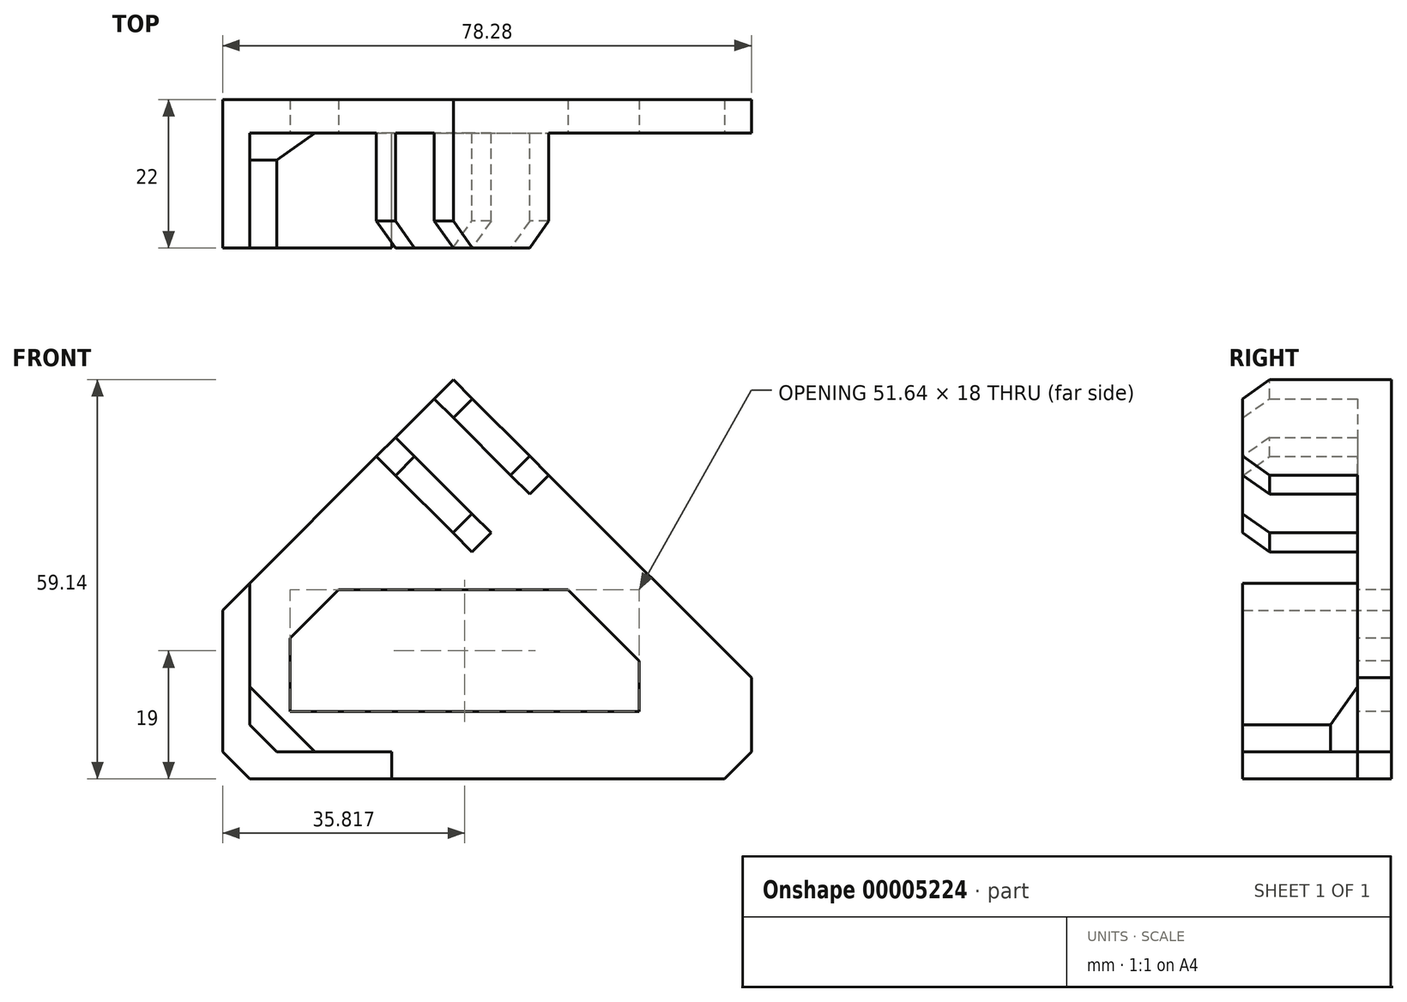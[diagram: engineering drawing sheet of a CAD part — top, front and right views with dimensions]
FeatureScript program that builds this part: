
annotation { "Feature Type Name" : "Feature", "Feature Type Description" : "" }
export const myFeature = defineFeature(function(context is Context, id is Id, definition is map)
    precondition{}
    {
        {
            var Q0;
            Q0=qCreatedBy(makeId("Front.planeOp"),FACE);
            var sketch = newSketch(context, id + "F0", { "sketchPlane" : qUnion([Q0])});
            skLineSegment(sketch, "E0", {"start": v(0, 0) * mm, "end": v(-75.51, 75.51) * mm, "construction": true});
            skLineSegment(sketch, "E1", {"start": v(0, 0) * mm, "end": v(-130.95, 0) * mm, "construction": true});
            skLineSegment(sketch, "E2", {"start": v(-59.14, 59.14) * mm, "end": v(-93.28, 25) * mm});
            skLineSegment(sketch, "E3", {"start": v(-93.28, 25) * mm, "end": v(-93.28, 0) * mm});
            skLineSegment(sketch, "E4", {"start": v(-93.28, 0) * mm, "end": v(-15, 0) * mm});
            skLineSegment(sketch, "E5", {"start": v(-15, 0) * mm, "end": v(-15, 15) * mm});
            skLineSegment(sketch, "E6", {"start": v(-15, 15) * mm, "end": v(-59.14, 59.14) * mm});
            skPoint(sketch, "E7", {"position": v(-45, 45) * mm});
            skSolve(sketch);
        }
        {
            var Q0;
            Q0 = qSketchRegion(id + "F0", true);
            extrude(context, id + "F1", {"entities" : qUnion([Q0]), "depth" : 5 * mm});
        }
        {
            var Q0;
            Q0=makeQuery(id+"F1.opExtrude","CAP_FACE",FACE,{"disambiguationData":[OSD([sQuery(id+"F0.wireOp",EDGE,"E2"),sQuery(id+"F0.wireOp",EDGE,"E3"),sQuery(id+"F0.wireOp",EDGE,"E4"),sQuery(id+"F0.wireOp",EDGE,"E5"),sQuery(id+"F0.wireOp",EDGE,"E6")])],"isStart":false});
            var sketch = newSketch(context, id + "F2", { "sketchPlane" : qUnion([Q0])});
            skLineSegment(sketch, "E8", {"start": v(-59.14, 59.14) * mm, "end": v(-61.97, 56.31) * mm});
            skLineSegment(sketch, "E9", {"start": v(-61.97, 56.31) * mm, "end": v(-47.83, 42.17) * mm});
            skLineSegment(sketch, "E10", {"start": v(-47.83, 42.17) * mm, "end": v(-45, 45) * mm});
            skLineSegment(sketch, "E11", {"start": v(-45, 45) * mm, "end": v(-59.14, 59.14) * mm});
            skLineSegment(sketch, "E12", {"start": v(-64.83, 53.45) * mm, "end": v(-26.8, 15.42) * mm, "construction": true});
            skLineSegment(sketch, "E13.MirrorCS", {"start": v(-70.53, 47.76) * mm, "end": v(-67.7, 50.59) * mm});
            skLineSegment(sketch, "E14.MirrorCS", {"start": v(-56.38, 33.62) * mm, "end": v(-70.53, 47.76) * mm});
            skLineSegment(sketch, "E15.MirrorCS", {"start": v(-53.56, 36.44) * mm, "end": v(-56.38, 33.62) * mm});
            skLineSegment(sketch, "E16.MirrorCS", {"start": v(-67.7, 50.59) * mm, "end": v(-53.56, 36.44) * mm});
            skLineSegment(sketch, "E17", {"start": v(-93.28, 25) * mm, "end": v(-93.28, 0) * mm});
            skLineSegment(sketch, "E18", {"start": v(-93.28, 0) * mm, "end": v(-68.28, 0) * mm});
            skLineSegment(sketch, "E19", {"start": v(-68.28, 0) * mm, "end": v(-68.28, 4) * mm});
            skLineSegment(sketch, "E20", {"start": v(-68.28, 4) * mm, "end": v(-89.28, 4) * mm});
            skLineSegment(sketch, "E21", {"start": v(-89.28, 4) * mm, "end": v(-89.28, 29) * mm});
            skLineSegment(sketch, "E22", {"start": v(-89.28, 29) * mm, "end": v(-93.28, 25) * mm});
            skSolve(sketch);
        }
        {
            var Q0;
            Q0 = qSketchRegion(id + "F2", true);
            extrude(context, id + "F3", {"entities" : qUnion([Q0]), "operationType" : NewBodyOperationType.ADD, "depth" : 17 * mm});
        }
        {
            var Q0;
            Q0=makeQuery(id+"F3.opExtrude","CAP_EDGE",EDGE,{"disambiguationData":[OSD([sQuery(id+"F2.wireOp",EDGE,"E8")])],"isStart":false});
            var Q1;
            Q1=makeQuery(id+"F3.opExtrude","CAP_EDGE",EDGE,{"disambiguationData":[OSD([sQuery(id+"F2.wireOp",EDGE,"E10")])],"isStart":false});
            var Q2;
            Q2=makeQuery(id+"F3.opExtrude","CAP_EDGE",EDGE,{"disambiguationData":[OSD([sQuery(id+"F2.wireOp",EDGE,"E13.MirrorCS")])],"isStart":false});
            var Q3;
            Q3=makeQuery(id+"F3.opExtrude","CAP_EDGE",EDGE,{"disambiguationData":[OSD([sQuery(id+"F2.wireOp",EDGE,"E15.MirrorCS")])],"isStart":false});
            var Q4;
            Q4=makeQuery(id+"F1.opExtrude","SWEPT_EDGE",EDGE,{"disambiguationData":[OSD([sQuery(id+"F0.wireOp",EDGE,"E4"),sQuery(id+"F0.wireOp",EDGE,"E5")])]});
            var Q5;
            Q5=makeQuery(id+"F1.opExtrude","SWEPT_EDGE",EDGE,{"disambiguationData":[OSD([sQuery(id+"F0.wireOp",EDGE,"E3"),sQuery(id+"F0.wireOp",EDGE,"E4")])]});
            var Q6;
            Q6=makeQuery(id+"F3.opExtrude","CAP_EDGE",EDGE,{"disambiguationData":[OSD([sQuery(id+"F2.wireOp",EDGE,"E14.MirrorCS")])],"isStart":true});
            var Q7;
            Q7=makeQuery(id+"F3.opExtrude","SWEPT_EDGE",EDGE,{"disambiguationData":[OSD([sQuery(id+"F2.wireOp",EDGE,"E20"),sQuery(id+"F2.wireOp",EDGE,"E21")])]});
            chamfer(context, id + "F4", {"entities" : qUnion([Q0, Q1, Q2, Q3, Q4, Q5, Q6, Q7]), "width" : 4 * mm, "tangentPropagation" : true});
        }
        {
            var Q0;
            Q0=makeQuery(id+"F1.opExtrude","CAP_FACE",FACE,{"disambiguationData":[OSD([sQuery(id+"F0.wireOp",EDGE,"E2"),sQuery(id+"F0.wireOp",EDGE,"E3"),sQuery(id+"F0.wireOp",EDGE,"E4"),sQuery(id+"F0.wireOp",EDGE,"E5"),sQuery(id+"F0.wireOp",EDGE,"E6")])],"isStart":false});
            var sketch = newSketch(context, id + "F5", { "sketchPlane" : qUnion([Q0])});
            skLineSegment(sketch, "E23", {"start": v(-83.28, 20.86) * mm, "end": v(-83.28, 10) * mm});
            skLineSegment(sketch, "E24", {"start": v(-83.28, 10) * mm, "end": v(-31.64, 10) * mm});
            skLineSegment(sketch, "E25", {"start": v(-31.64, 10) * mm, "end": v(-31.64, 17.5) * mm});
            skLineSegment(sketch, "E26", {"start": v(-31.64, 17.5) * mm, "end": v(-42.14, 28) * mm});
            skLineSegment(sketch, "E27", {"start": v(-42.14, 28) * mm, "end": v(-76.14, 28) * mm});
            skLineSegment(sketch, "E28", {"start": v(-76.14, 28) * mm, "end": v(-83.28, 20.86) * mm});
            skSolve(sketch);
        }
        {
            var Q0;
            Q0 = qSketchRegion(id + "F5", true);
            extrude(context, id + "F6", {"entities" : qUnion([Q0]), "operationType" : NewBodyOperationType.REMOVE, "endBound" : BoundingType.THROUGH_ALL, "oppositeDirection" : true, "depth" : 25 * mm});
        }
        {
            var Q0;
            Q0=makeQuery(id+"F3.opExtrude","CAP_EDGE",EDGE,{"disambiguationData":[OSD([sQuery(id+"F2.wireOp",EDGE,"E21")])],"isStart":true});
            var Q1;
            Q1=makeQuery(id+"F4.opChamfer","BLEND_EDGE",EDGE,{"blendedFrom":[makeQuery(id+"F3.opExtrude","SWEPT_EDGE",EDGE,{"disambiguationData":[OSD([sQuery(id+"F2.wireOp",EDGE,"E20"),sQuery(id+"F2.wireOp",EDGE,"E21")])]}),makeQuery(id+"F1.opExtrude","CAP_FACE",FACE,{"disambiguationData":[OSD([sQuery(id+"F0.wireOp",EDGE,"E2"),sQuery(id+"F0.wireOp",EDGE,"E3"),sQuery(id+"F0.wireOp",EDGE,"E4"),sQuery(id+"F0.wireOp",EDGE,"E5"),sQuery(id+"F0.wireOp",EDGE,"E6")])],"isStart":false})],"blendedInto":[makeQuery(id+"F1.opExtrude","CAP_FACE",FACE,{"disambiguationData":[OSD([sQuery(id+"F0.wireOp",EDGE,"E2"),sQuery(id+"F0.wireOp",EDGE,"E3"),sQuery(id+"F0.wireOp",EDGE,"E4"),sQuery(id+"F0.wireOp",EDGE,"E5"),sQuery(id+"F0.wireOp",EDGE,"E6")])],"isStart":false})]});
            var Q2;
            Q2=makeQuery(id+"F3.opExtrude","CAP_EDGE",EDGE,{"disambiguationData":[OSD([sQuery(id+"F2.wireOp",EDGE,"E20")])],"isStart":true});
            chamfer(context, id + "F7", {"entities" : qUnion([Q0, Q1, Q2]), "width" : 4 * mm, "tangentPropagation" : true});
        }
    });
